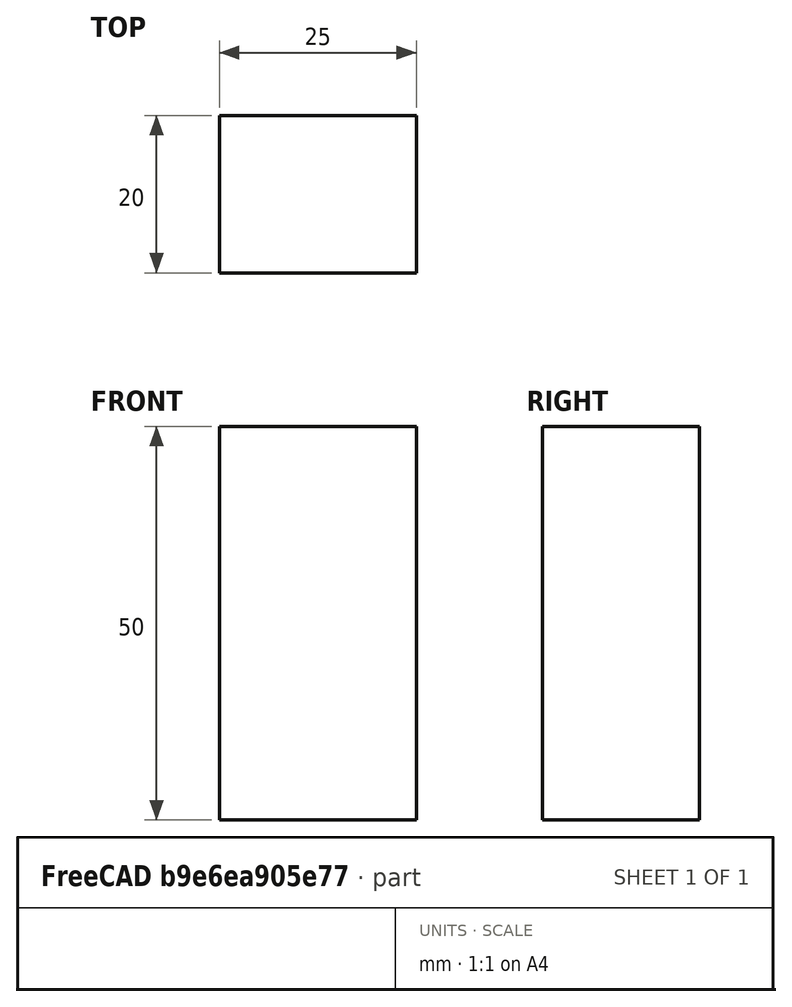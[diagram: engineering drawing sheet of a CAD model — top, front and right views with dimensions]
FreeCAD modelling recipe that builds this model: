
FCSTD DOCUMENT  (FreeCAD 0.15R4671 (Git))
Label: Flat Bar 25x20 EN10058 S235JR
License: All rights reserved
LicenseURL: http://en.wikipedia.org/wiki/All_rights_reserved
objects: Sketcher::SketchObject×1, Part::Extrusion×1
note: 2 computed .brp shape members not serialized (recipe doc carries the construction recipe); baked Part::Feature solids carry a one-line shape summary decoded from their .brp

FEATURE [Sketcher::SketchObject] Sketch
  sketch-geometry (4):
    g0: LineSegment StartX=-12.5 StartY=-10 StartZ=0 EndX=12.5 EndY=-10 EndZ=0
    g1: LineSegment StartX=12.5 StartY=-10 StartZ=0 EndX=12.5 EndY=10 EndZ=0
    g2: LineSegment StartX=12.5 StartY=10 StartZ=0 EndX=-12.5 EndY=10 EndZ=0
    g3: LineSegment StartX=-12.5 StartY=10 StartZ=0 EndX=-12.5 EndY=-10 EndZ=0
  constraints (12):
    c: Coincident(g0,g1)
    c: Coincident(g1,g2)
    c: Coincident(g2,g3)
    c: Coincident(g3,g0)
    c: Horizontal(g0)
    c: Horizontal(g2)
    c: Vertical(g1)
    c: Vertical(g3)
    c: Symmetric(g1,g2,g-2)
    c: Symmetric(g0,g1,g-1)
    c: DistanceY(g1) = 20
    c: DistanceX(g0) = 25
FEATURE [Part::Extrusion] Extrude  label="Flat Bar 25x20 EN10058 S235JR"
  Base = -> Sketch
  Dir = (0,0,50)
  Solid = true
